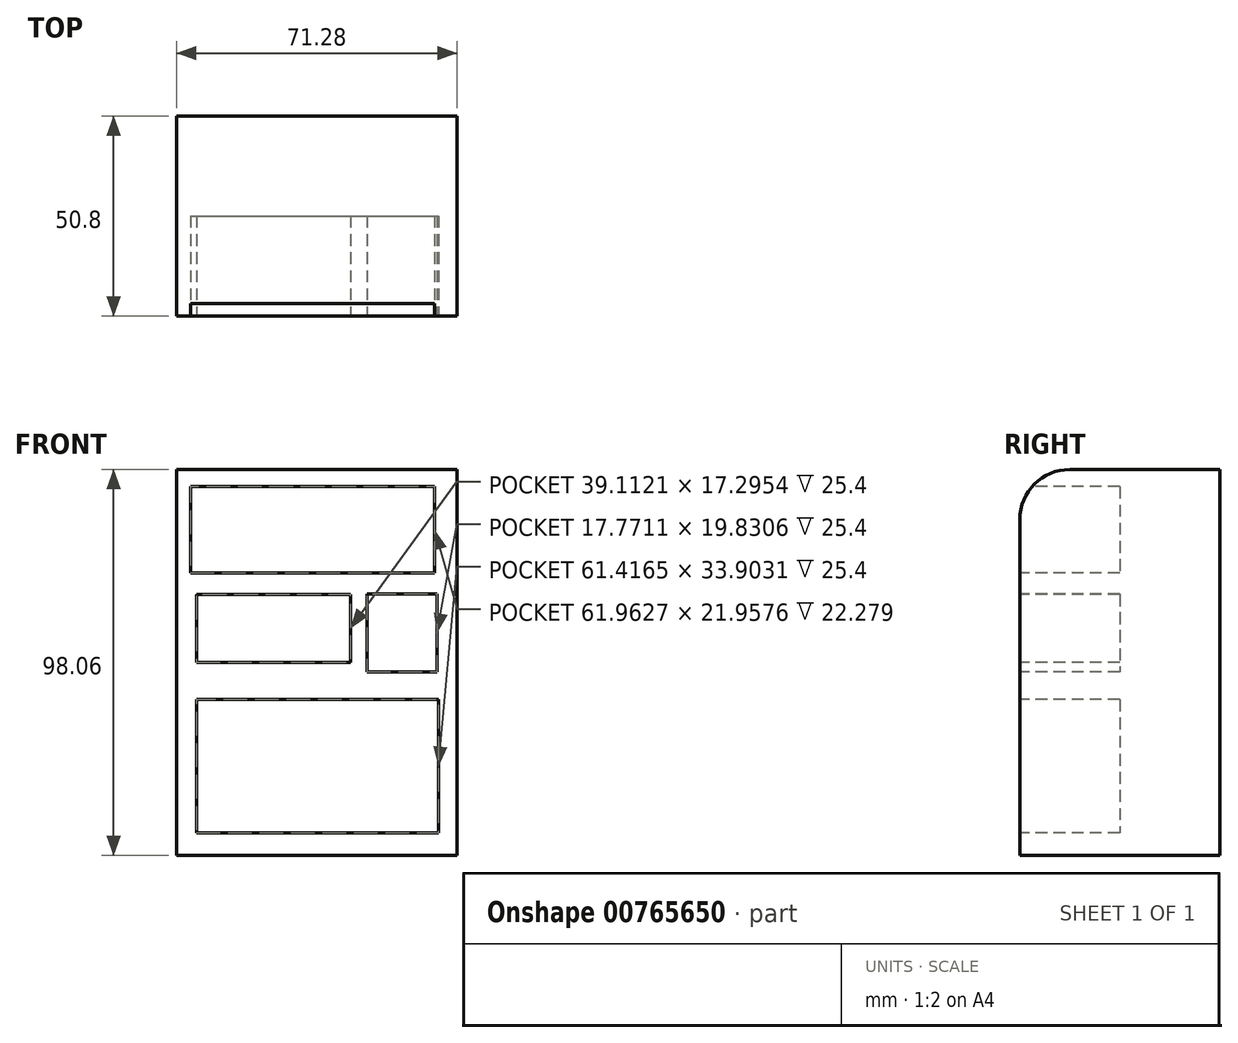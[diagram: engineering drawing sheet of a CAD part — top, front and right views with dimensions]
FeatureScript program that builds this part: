
annotation { "Feature Type Name" : "Feature", "Feature Type Description" : "" }
export const myFeature = defineFeature(function(context is Context, id is Id, definition is map)
    precondition{}
    {
        {
            var Q0;
            Q0=qCreatedBy(makeId("Front.planeOp"),FACE);
            var sketch = newSketch(context, id + "F0", { "sketchPlane" : qUnion([Q0])});
            skLineSegment(sketch, "E0.bottom", {"start": v(-35.64, 49.03) * mm, "end": v(35.64, 49.03) * mm});
            skLineSegment(sketch, "E0.top", {"start": v(-35.64, -49.03) * mm, "end": v(35.64, -49.03) * mm});
            skLineSegment(sketch, "E0.left", {"start": v(-35.64, 49.03) * mm, "end": v(-35.64, -49.03) * mm});
            skLineSegment(sketch, "E0.right", {"start": v(35.64, 49.03) * mm, "end": v(35.64, -49.03) * mm});
            skLineSegment(sketch, "E1", {"start": v(-35.64, 49.03) * mm, "end": v(35.64, -49.03) * mm, "construction": true});
            skLineSegment(sketch, "E2", {"start": v(-35.64, 0) * mm, "end": v(35.64, 0) * mm});
            skLineSegment(sketch, "E3.bottom", {"start": v(-29.88, 41.1) * mm, "end": v(28.65, 41.1) * mm});
            skLineSegment(sketch, "E3.top", {"start": v(-29.88, 5.08) * mm, "end": v(28.65, 5.08) * mm});
            skLineSegment(sketch, "E3.left", {"start": v(-29.88, 41.1) * mm, "end": v(-29.88, 5.08) * mm});
            skLineSegment(sketch, "E3.right", {"start": v(28.65, 41.1) * mm, "end": v(28.65, 5.08) * mm});
            skLineSegment(sketch, "E4.bottom", {"start": v(-30.16, -9.24) * mm, "end": v(30.75, -9.24) * mm});
            skLineSegment(sketch, "E4.top", {"start": v(-30.16, -42.3) * mm, "end": v(30.75, -42.3) * mm});
            skLineSegment(sketch, "E4.left", {"start": v(-30.16, -9.24) * mm, "end": v(-30.16, -42.3) * mm});
            skLineSegment(sketch, "E4.right", {"start": v(30.75, -9.24) * mm, "end": v(30.75, -42.3) * mm});
            skSolve(sketch);
        }
        {
            var Q0;
            Q0=makeQuery(id+"F0.imprint","IMPRINT",FACE,{"disambiguationData":[TD([[makeQuery(id+"F0.imprint","IMPRINT",EDGE,{"derivedFrom":sQuery(id+"F0.wireOp",EDGE,"E4.bottom")}),-1.0]])]});
            var Q1;
            Q1=makeQuery(id+"F0.imprint","IMPRINT",FACE,{"disambiguationData":[TD([[makeQuery(id+"F0.imprint","IMPRINT",EDGE,{"derivedFrom":sQuery(id+"F0.wireOp",EDGE,"E3.bottom")}),-1.0]])]});
            var Q2;
            {var subQ2=sQuery(id+"F0.wireOp",EDGE,"E0.bottom");Q2=makeQuery(id+"F0.imprint","IMPRINT",FACE,{"disambiguationData":[TD([[makeQuery(id+"F0.imprint","IMPRINT",EDGE,{"derivedFrom":subQ2}),-1.0]])]});}
            var Q3;
            {var subQ1=sQuery(id+"F0.wireOp",EDGE,"E0.top");Q3=makeQuery(id+"F0.imprint","IMPRINT",FACE,{"disambiguationData":[TD([[makeQuery(id+"F0.imprint","IMPRINT",EDGE,{"derivedFrom":subQ1}),1.0]])]});}
            var Q4;
            Q4=sQuery(id+"F0.wireOp",EDGE,"E0.bottom");
            var Q5;
            Q5=sQuery(id+"F0.wireOp",EDGE,"E0.right");
            var Q6;
            Q6=sQuery(id+"F0.wireOp",EDGE,"E0.left");
            var Q7;
            Q7=sQuery(id+"F0.wireOp",EDGE,"E0.top");
            extrude(context, id + "F1", {"entities" : qUnion([Q0, Q1, Q2, Q3]), "surfaceEntities" : qUnion([Q4, Q5, Q6, Q7]), "depth" : 50.8 * mm, "offsetDistance" : 25.4 * mm});
        }
        {
            var Q0;
            Q0=makeQuery(id+"F1.opExtrude","CAP_FACE",FACE,{"disambiguationData":[OSD([sQuery(id+"F0.wireOp",EDGE,"E0.bottom"),sQuery(id+"F0.wireOp",EDGE,"E0.top"),sQuery(id+"F0.wireOp",EDGE,"E0.left"),sQuery(id+"F0.wireOp",EDGE,"E0.right")])],"isStart":false});
            var sketch = newSketch(context, id + "F2", { "sketchPlane" : qUnion([Q0])});
            skLineSegment(sketch, "E5.bottom", {"start": v(-32.03, 44.67) * mm, "end": v(29.93, 44.67) * mm});
            skLineSegment(sketch, "E5.top", {"start": v(-32.03, 22.7) * mm, "end": v(29.93, 22.7) * mm});
            skLineSegment(sketch, "E5.left", {"start": v(-32.03, 44.67) * mm, "end": v(-32.03, 22.7) * mm});
            skLineSegment(sketch, "E5.right", {"start": v(29.93, 44.67) * mm, "end": v(29.93, 22.7) * mm});
            skLineSegment(sketch, "E6.bottom", {"start": v(-30.53, 17.3) * mm, "end": v(8.58, 17.3) * mm});
            skLineSegment(sketch, "E6.top", {"start": v(-30.53, 0) * mm, "end": v(8.58, 0) * mm});
            skLineSegment(sketch, "E6.left", {"start": v(-30.53, 17.3) * mm, "end": v(-30.53, 0) * mm});
            skLineSegment(sketch, "E6.right", {"start": v(8.58, 17.3) * mm, "end": v(8.58, 0) * mm});
            skLineSegment(sketch, "E7.bottom", {"start": v(12.78, 17.43) * mm, "end": v(30.56, 17.43) * mm});
            skLineSegment(sketch, "E7.top", {"start": v(12.78, -2.4) * mm, "end": v(30.56, -2.4) * mm});
            skLineSegment(sketch, "E7.left", {"start": v(12.78, 17.43) * mm, "end": v(12.78, -2.4) * mm});
            skLineSegment(sketch, "E7.right", {"start": v(30.56, 17.43) * mm, "end": v(30.56, -2.4) * mm});
            skLineSegment(sketch, "E8.bottom", {"start": v(-30.53, -9.42) * mm, "end": v(30.89, -9.42) * mm});
            skLineSegment(sketch, "E8.top", {"start": v(-30.53, -43.32) * mm, "end": v(30.89, -43.32) * mm});
            skLineSegment(sketch, "E8.left", {"start": v(-30.53, -9.42) * mm, "end": v(-30.53, -43.32) * mm});
            skLineSegment(sketch, "E8.right", {"start": v(30.89, -9.42) * mm, "end": v(30.89, -43.32) * mm});
            skSolve(sketch);
        }
        {
            var Q0;
            Q0=makeQuery(id+"F2.imprint","IMPRINT",FACE,{"disambiguationData":[TD([[makeQuery(id+"F2.imprint","IMPRINT",EDGE,{"derivedFrom":sQuery(id+"F2.wireOp",EDGE,"E6.bottom")}),-1.0]])]});
            var Q1;
            Q1=makeQuery(id+"F2.imprint","IMPRINT",FACE,{"disambiguationData":[TD([[makeQuery(id+"F2.imprint","IMPRINT",EDGE,{"derivedFrom":sQuery(id+"F2.wireOp",EDGE,"E7.bottom")}),-1.0]])]});
            var Q2;
            Q2=makeQuery(id+"F2.imprint","IMPRINT",FACE,{"disambiguationData":[TD([[makeQuery(id+"F2.imprint","IMPRINT",EDGE,{"derivedFrom":sQuery(id+"F2.wireOp",EDGE,"E8.bottom")}),-1.0]])]});
            var Q3;
            Q3=makeQuery(id+"F2.imprint","IMPRINT",FACE,{"disambiguationData":[TD([[makeQuery(id+"F2.imprint","IMPRINT",EDGE,{"derivedFrom":sQuery(id+"F2.wireOp",EDGE,"E5.bottom")}),-1.0]])]});
            extrude(context, id + "F3", {"entities" : qUnion([Q0, Q1, Q2, Q3]), "operationType" : NewBodyOperationType.REMOVE, "oppositeDirection" : true, "depth" : 25.4 * mm, "offsetDistance" : 25.4 * mm});
        }
        {
            var Q0;
            Q0=makeQuery(id+"F1.opExtrude","CAP_EDGE",EDGE,{"disambiguationData":[OSD([sQuery(id+"F0.wireOp",EDGE,"E0.bottom")])],"isStart":false});
            fillet(context, id + "F4", {"entities" : qUnion([Q0]), "radius" : 12.7 * mm, "tangentPropagation" : true, "allowEdgeOverflow" : false});
        }
    });
